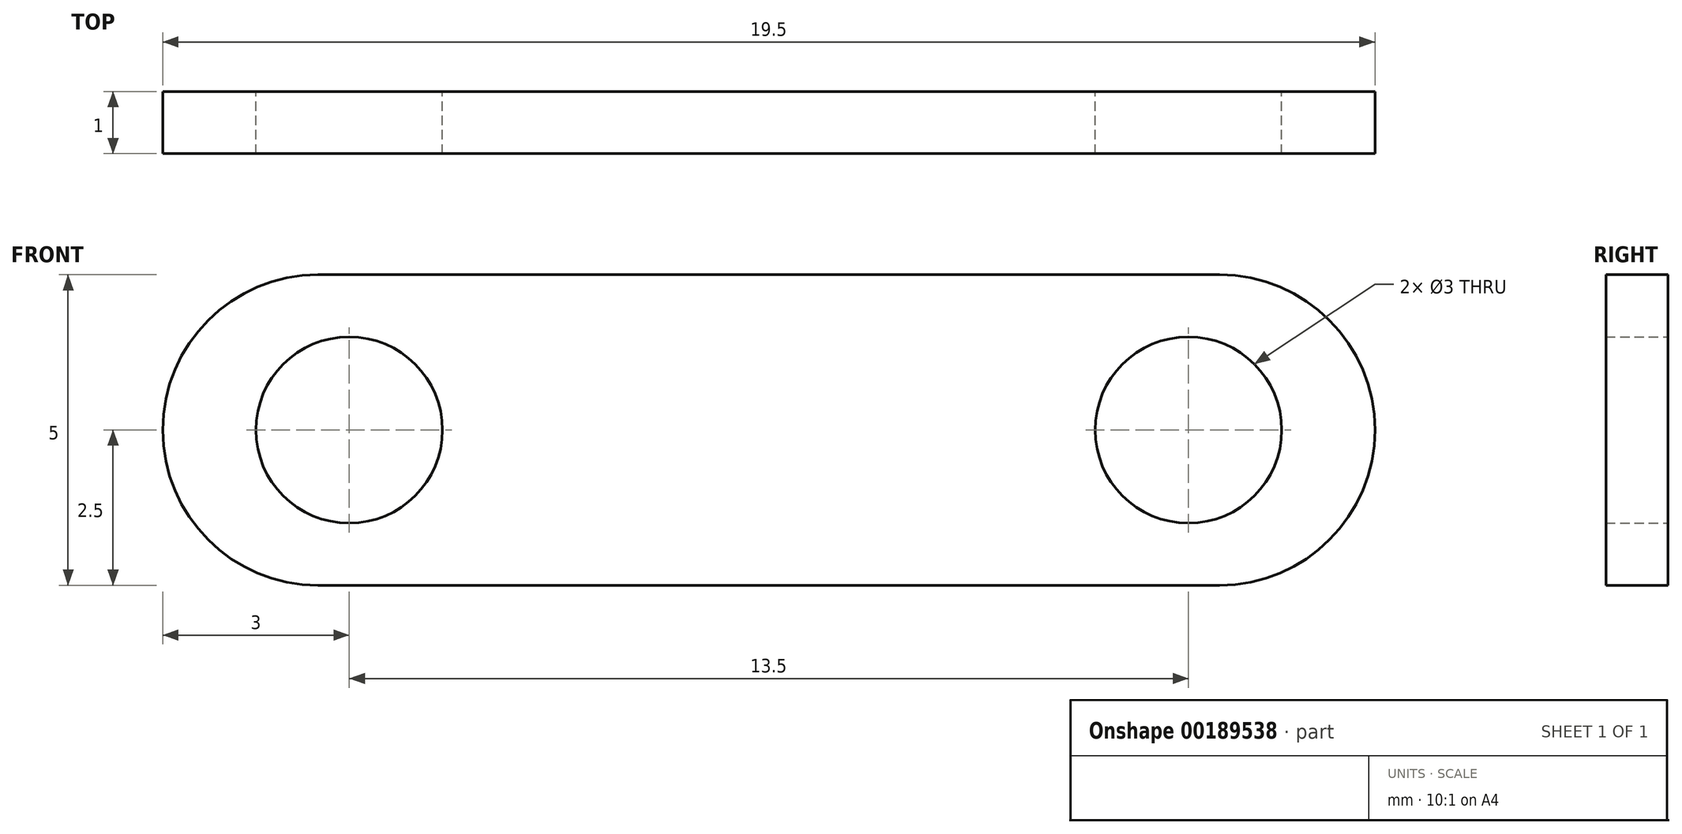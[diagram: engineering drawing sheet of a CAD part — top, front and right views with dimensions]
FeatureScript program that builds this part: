
annotation { "Feature Type Name" : "Feature", "Feature Type Description" : "" }
export const myFeature = defineFeature(function(context is Context, id is Id, definition is map)
    precondition{}
    {
        {
            var Q0;
            Q0=qCreatedBy(makeId("Front.planeOp"),FACE);
            var sketch = newSketch(context, id + "F0", { "sketchPlane" : qUnion([Q0])});
            skLineSegment(sketch, "E0.bottom", {"start": v(0, 0) * mm, "end": v(19.5, 0) * mm});
            skLineSegment(sketch, "E0.top", {"start": v(0, 5) * mm, "end": v(19.5, 5) * mm});
            skLineSegment(sketch, "E0.left", {"start": v(0, 0) * mm, "end": v(0, 5) * mm});
            skLineSegment(sketch, "E0.right", {"start": v(19.5, 0) * mm, "end": v(19.5, 5) * mm});
            skCircle(sketch, "E1", {"center": v(3, 2.5) * mm, "radius": 1.5 * mm});
            skCircle(sketch, "E2", {"center": v(16.5, 2.5) * mm, "radius": 1.5 * mm});
            skSolve(sketch);
        }
        {
            var Q0;
            Q0=makeQuery(id+"F0.imprint","IMPRINT",FACE,{"disambiguationData":[TD([[makeQuery(id+"F0.imprint","IMPRINT",EDGE,{"derivedFrom":sQuery(id+"F0.wireOp",EDGE,"E0.bottom")}),1.0]])]});
            extrude(context, id + "F1", {"entities" : qUnion([Q0]), "depth" : 1 * mm});
        }
        {
            var Q0;
            Q0=makeQuery(id+"F1.opExtrude","SWEPT_EDGE",EDGE,{"disambiguationData":[OSD([sQuery(id+"F0.wireOp",EDGE,"E0.top"),sQuery(id+"F0.wireOp",EDGE,"E0.left")])]});
            var Q1;
            Q1=makeQuery(id+"F1.opExtrude","SWEPT_EDGE",EDGE,{"disambiguationData":[OSD([sQuery(id+"F0.wireOp",EDGE,"E0.bottom"),sQuery(id+"F0.wireOp",EDGE,"E0.left")])]});
            var Q2;
            Q2=makeQuery(id+"F1.opExtrude","SWEPT_EDGE",EDGE,{"disambiguationData":[OSD([sQuery(id+"F0.wireOp",EDGE,"E0.top"),sQuery(id+"F0.wireOp",EDGE,"E0.right")])]});
            var Q3;
            Q3=makeQuery(id+"F1.opExtrude","SWEPT_EDGE",EDGE,{"disambiguationData":[OSD([sQuery(id+"F0.wireOp",EDGE,"E0.bottom"),sQuery(id+"F0.wireOp",EDGE,"E0.right")])]});
            fillet(context, id + "F2", {"entities" : qUnion([Q0, Q1, Q2, Q3]), "radius" : 2.5 * mm, "tangentPropagation" : true, "allowEdgeOverflow" : false});
        }
    });
